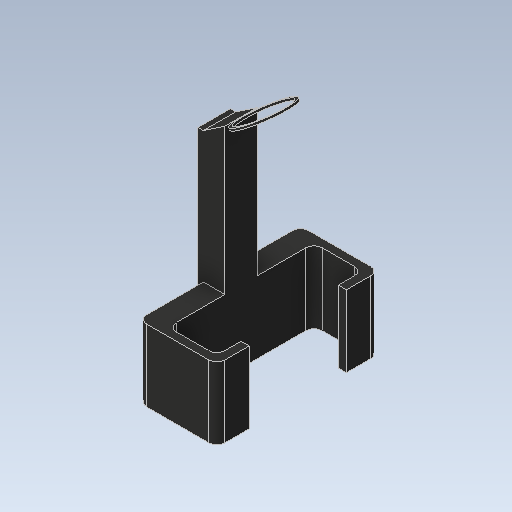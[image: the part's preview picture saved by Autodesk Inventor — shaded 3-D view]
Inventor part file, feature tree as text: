
AUTODESK INVENTOR PART (.ipt)
format: ipt  version: 2021 (Build 250183000, 183)  size: 385,536 bytes
history: native  units: in
note: dims shown in document units (in); Inventor stores cm internally (conversion verified against a paired STEP export)
features: sketch x35, extrude x22, mirror x8, direct_edit x1, other x1
ambient origin geometry x8: Origin, YZ Plane, XZ Plane, XY Plane, X Axis, Y Axis, Z Axis, Center Point
bodies: Solid1 (feature_tree)
feature tree (67):
  extrude  "Extrusion1"  Depth=1.063in
  extrude  "Extrusion2"  Depth=17.7165in
  extrude  "Extrusion3"  Depth=10.6299in
  extrude  "Extrusion4"  Depth=1.063in
  mirror  "Mirror1"
  sketch  "Sketch5"  dims[d10=15.748in d11=0.0in d12=4.7244in]
  extrude  "Extrusion5"  Depth=4.7244in
  extrude  "Extrusion6"  Depth=15.748in TaperAngle=0.0deg
  mirror  "Mirror2"
  sketch  "Sketch8"  dims[d18=0.1575in d19=0.0in d20=0.7874in]
  sketch  "Sketch9"  dims[d21=11.811in d22=0.0in d23=3.5433in]
  sketch  "Sketch10"  dims[d24=0.5906in d25=0.0in d26=0.5906in d27=0.0in]
  extrude  "Extrusion7"  Depth=3.5433in
  mirror  "Mirror3"
  extrude  "Extrusion8"  Depth=0.7874in
  mirror  "Mirror4"
  extrude  "Extrusion9"  Depth=3.5433in
  mirror  "Mirror5"
  extrude  "Extrusion10"  Depth=0.5906in TaperAngle=0.0deg
  sketch  "Sketch15"  dims[d40=0.5906in d41=5.2362in d42=0.0in]
  sketch  "Sketch16"  dims[d43=0.7874in d44=0.3937in d45=0.3937in d46=33.3071in]
  extrude  "Extrusion11"  Depth=7.874in TaperAngle=0.0deg
  mirror  "Mirror6"
  extrude  "Extrusion12"  Depth=7.874in TaperAngle=0.0deg
  mirror  "Mirror7"
  extrude  "Extrusion13"  Depth=5.2362in TaperAngle=0.0deg
  mirror  "Mirror8"
  direct_edit  "Direct Edit1"
  sketch  "Sketch19"  dims[d54=5.0787in d55=0.0in d56=5.0787in d57=0.0in]
  sketch  "Sketch20"  dims[d58=3.5433in d59=1.9685in]
  sketch  "Sketch21"  dims[d60=1.5748in d61=0.0in d62=1.5748in]
  sketch  "Sketch22"  dims[d63=1.5748in d64=0.0in d65=3.5433in]
  sketch  "Sketch23"  dims[d66=0.7874in d67=0.0in]
  extrude  "Extrusion14"  Depth=5.2362in TaperAngle=0.0deg
  extrude  "Extrusion15"  Depth=5.2362in TaperAngle=0.0deg
  extrude  "Extrusion16"  Depth=0.3937in
  extrude  "Extrusion17"  Depth=5.0787in TaperAngle=0.0deg
  extrude  "Extrusion18"  Depth=5.0787in TaperAngle=0.0deg
  sketch  "Sketch28"
  sketch  "Sketch29"
  extrude  "Extrusion19"  Depth=5.0787in TaperAngle=0.0deg
  extrude  "Extrusion20"  Depth=3.5433in
  extrude  "Extrusion21"  Depth=1.5748in
  extrude  "Extrusion22"  Depth=3.5433in
  sketch  "Sketch34"
  sketch  "Sketch35"
  sketch  "Sketch1"  dims[d0=16.6535in d1=1.063in]
  sketch  "Sketch2"  dims[d2=1.5748in d3=17.7165in]
  sketch  "Sketch3"  dims[d4=11.811in d5=0.0in d6=10.6299in]
  sketch  "Sketch4"  dims[d7=10.375in d8=0.0in d9=1.063in]
  sketch  "Sketch6"  dims[d13=1.063in d14=15.748in d15=0.0in]
  sketch  "Sketch7"  dims[d16=1.9685in d17=3.5433in]
  sketch  "Sketch11"  dims[d28=0.7874in d29=7.874in d30=0.0in]
  sketch  "Sketch12"  dims[d31=0.5906in d32=7.874in d33=0.0in]
  sketch  "Sketch13"  dims[d34=0.5906in d35=5.2362in d36=0.0in]
  sketch  "Sketch14"  dims[d37=0.5906in d38=5.2362in d39=0.0in]
  sketch  "Sketch17"  dims[d47=0.7874in d48=5.0787in d49=0.0in]
  sketch  "Sketch18"  dims[d50=5.0787in d51=0.0in d52=5.0787in d53=0.0in]
  sketch  "Sketch24"  dims[d68=3.5433in]
  sketch  "Sketch25"  dims[d69=0.7874in d70=0.0in]
  sketch  "Sketch26"
  sketch  "Sketch27"
  sketch  "Sketch30"
  sketch  "Sketch31"
  sketch  "Sketch32"
  sketch  "Sketch33"
  other  "Scale1"
